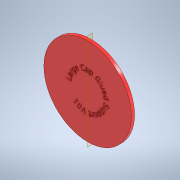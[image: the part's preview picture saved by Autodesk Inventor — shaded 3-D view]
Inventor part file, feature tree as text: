
AUTODESK INVENTOR PART (.ipt)
format: ipt  version: 2021.1 (Build 251245010, 245A)  size: 722,944 bytes
history: native  units: in
note: dims shown in document units (in); Inventor stores cm internally (conversion verified against a paired STEP export)
features: sketch x3, extrude x2, revolve x1, fillet x1, split x1
ambient origin geometry x8: Origin, YZ Plane, XZ Plane, XY Plane, X Axis, Y Axis, Z Axis, Center Point
bodies: Solid1 (feature_tree)
feature tree (8):
  extrude  "Extrusion1"  Depth=0.25in TaperAngle=0.0deg
  extrude  "Extrusion2"  Depth=0.05in TaperAngle=0.0deg
  revolve  "Revolution1"  [1 undecoded]
  fillet  "Fillet1"  Radius=0.5in
  split  "Split1"
  sketch  "Sketch1"  dims[d0=7.0in d1=0.25in d2=0.0in]
  sketch  "Sketch2"  dims[d3=3.0in d4=0.05in d5=0.0in]
  sketch  "Sketch5"  dims[d17=2.75in d18=0.125in d19=0.5in d20=90.0deg d21=0.0625in]
note: 1 required parameter value undecoded (feature->parameter linkage not recoverable at this tier; creation-order binding heuristic only, values carry confidence <= 0.55)
